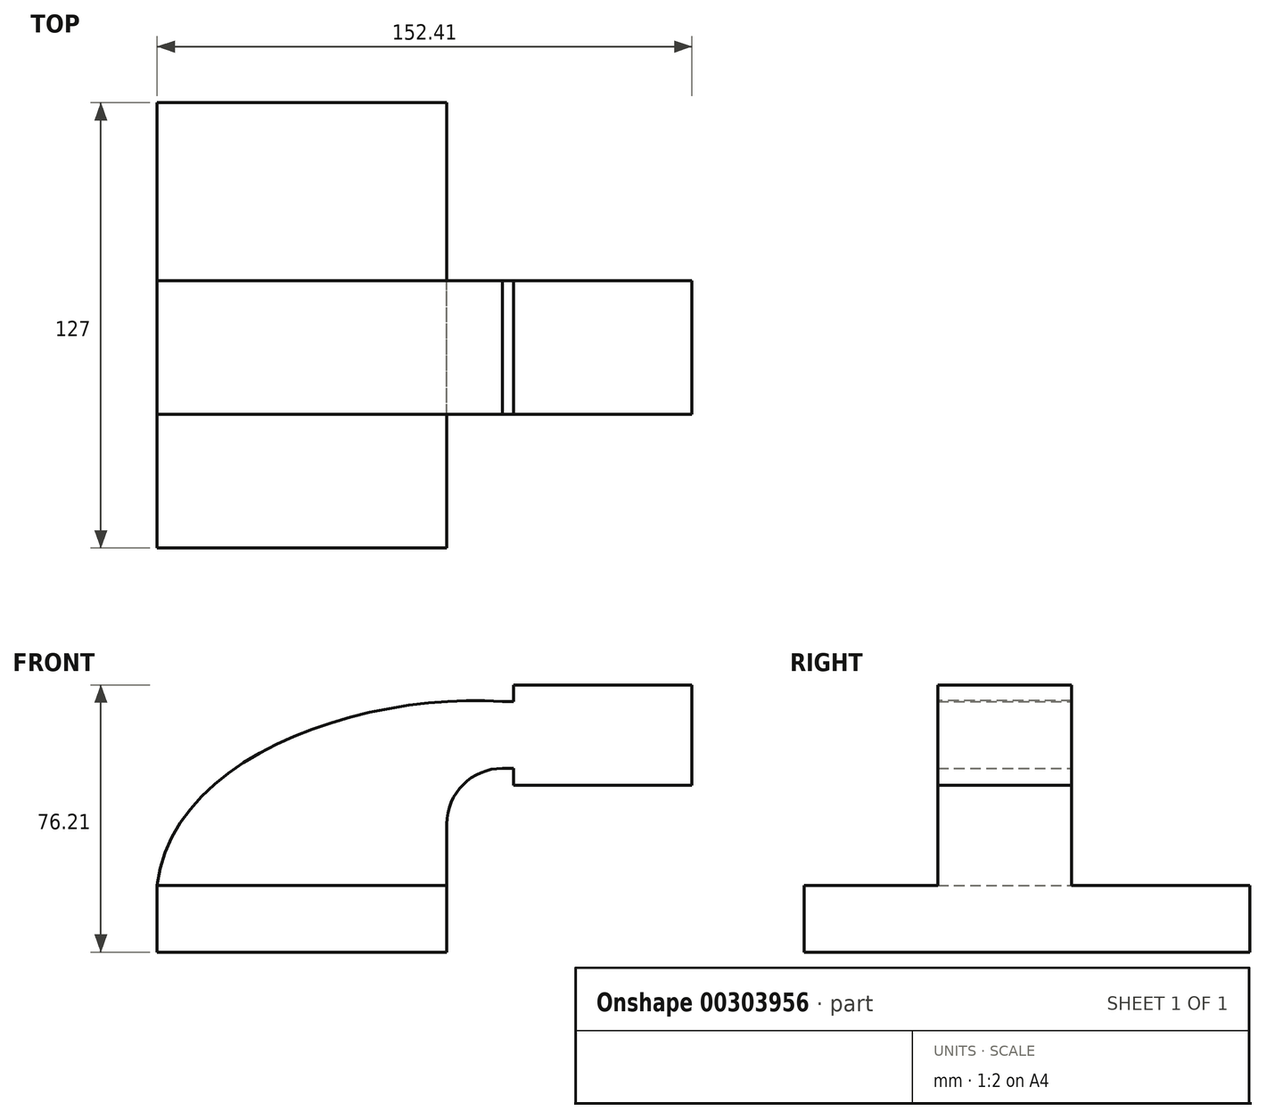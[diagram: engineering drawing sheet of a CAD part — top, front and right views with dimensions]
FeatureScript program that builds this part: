
annotation { "Feature Type Name" : "Feature", "Feature Type Description" : "" }
export const myFeature = defineFeature(function(context is Context, id is Id, definition is map)
    precondition{}
    {
        {
            var Q0;
            Q0=qCreatedBy(makeId("Front.planeOp"),FACE);
            var sketch = newSketch(context, id + "F0", { "sketchPlane" : qUnion([Q0])});
            skLineSegment(sketch, "E0.bottom", {"start": v(-41.28, 9.52) * mm, "end": v(41.27, 9.53) * mm});
            skLineSegment(sketch, "E0.top", {"start": v(-41.28, -9.53) * mm, "end": v(41.28, -9.53) * mm});
            skLineSegment(sketch, "E0.left", {"start": v(-41.28, 9.52) * mm, "end": v(-41.28, -9.53) * mm});
            skLineSegment(sketch, "E0.right", {"start": v(41.27, 9.53) * mm, "end": v(41.28, -9.52) * mm});
            skPoint(sketch, "E0.middle", {"position": v(0, 0) * mm});
            skLineSegment(sketch, "E1.bottom", {"start": v(60.32, 38.1) * mm, "end": v(111.12, 38.1) * mm});
            skLineSegment(sketch, "E1.top", {"start": v(60.32, 66.68) * mm, "end": v(111.12, 66.68) * mm});
            skLineSegment(sketch, "E1.left", {"start": v(60.32, 38.1) * mm, "end": v(60.32, 66.67) * mm});
            skLineSegment(sketch, "E1.right", {"start": v(111.12, 38.1) * mm, "end": v(111.12, 66.67) * mm});
            skPoint(sketch, "E1.middle", {"position": v(85.72, 52.39) * mm});
            skLineSegment(sketch, "E2", {"start": v(41.27, 9.53) * mm, "end": v(41.27, 27) * mm});
            skArc(sketch, "E3", {"start": v(41.27, 27) * mm, "mid": v(45.92, 38.23) * mm, "end": v(57.15, 42.88) * mm});
            skLineSegment(sketch, "E4", {"start": v(57.15, 42.88) * mm, "end": v(85.78, 42.88) * mm});
            skLineSegment(sketch, "E5.0", {"start": v(57.15, 61.93) * mm, "end": v(85.78, 61.93) * mm});
            skArc(sketch, "E5.1", {"start": v(22.22, 27) * mm, "mid": v(32.45, 51.7) * mm, "end": v(57.15, 61.93) * mm});
            skLineSegment(sketch, "E5.2", {"start": v(22.22, 9.53) * mm, "end": v(22.22, 27) * mm});
            skFitSpline(sketch, "E6", {"points": [v(-41.28, 9.53) * mm, v(57.15, 61.93) * mm], "startDerivative": vector(13.02, 112.94) * mm, "endDerivative": vector(114.48, -8.29) * mm});
            skSolve(sketch);
        }
        {
            var Q0;
            Q0=makeQuery(id+"F0.imprint","IMPRINT",FACE,{"disambiguationData":[TD([[makeQuery(id+"F0.imprint","IMPRINT",EDGE,{"derivedFrom":sQuery(id+"F0.wireOp",EDGE,"E0.top")}),1.0]])]});
            extrude(context, id + "F1", {"entities" : qUnion([Q0]), "endBound" : BoundingType.SYMMETRIC, "depth" : 127 * mm});
        }
        {
            var Q0;
            Q0 = qSketchRegion(id + "F0", true);
            extrude(context, id + "F2", {"entities" : qUnion([Q0]), "operationType" : NewBodyOperationType.ADD, "depth" : 25.4 * mm});
        }
        {
            var Q0;
            Q0 = qSketchRegion(id + "F0", true);
            extrude(context, id + "F3", {"entities" : qUnion([Q0]), "operationType" : NewBodyOperationType.ADD, "endBound" : BoundingType.SYMMETRIC, "depth" : 25.4 * mm});
        }
    });
